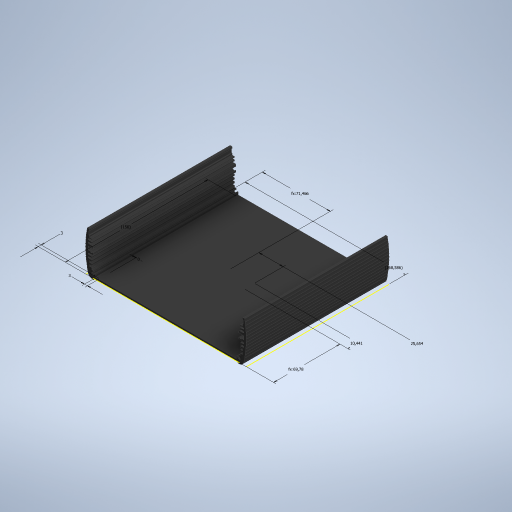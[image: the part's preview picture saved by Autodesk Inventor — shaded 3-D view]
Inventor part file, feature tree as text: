
AUTODESK INVENTOR PART (.ipt)
format: ipt  version: 2024.2 (Build 282272000, 272)  size: 572,416 bytes
history: native  units: mm
features: other x5, sketch x1, reference x1
ambient origin geometry x8: Origin, YZ Plane, XZ Plane, XY Plane, X Axis, Y Axis, Z Axis, Center Point
bodies: Solid1 (feature_tree), Volumenkörper1 (feature_tree)
feature tree (7):
  sketch  "Sketch1"  dims[d0=0.0mm d1=3.0mm d2=3.0mm d3=10.440924mm d4=69.779538mm d5=150.0mm d6=25.654376mm d7=168.586321mm d8=71.465973mm]
  reference  "Reference1"
  other  "<userpath>\Google Drive\Unicorn 2020\CAD_V2\Main_Assembly.iam"
  other  "Main_Assembly.iam"
  other  "Front_Panel_Assembly:1"
  other  "Front_Pane_Basel_Assembly:1"
  other  "DI 1600:1"
